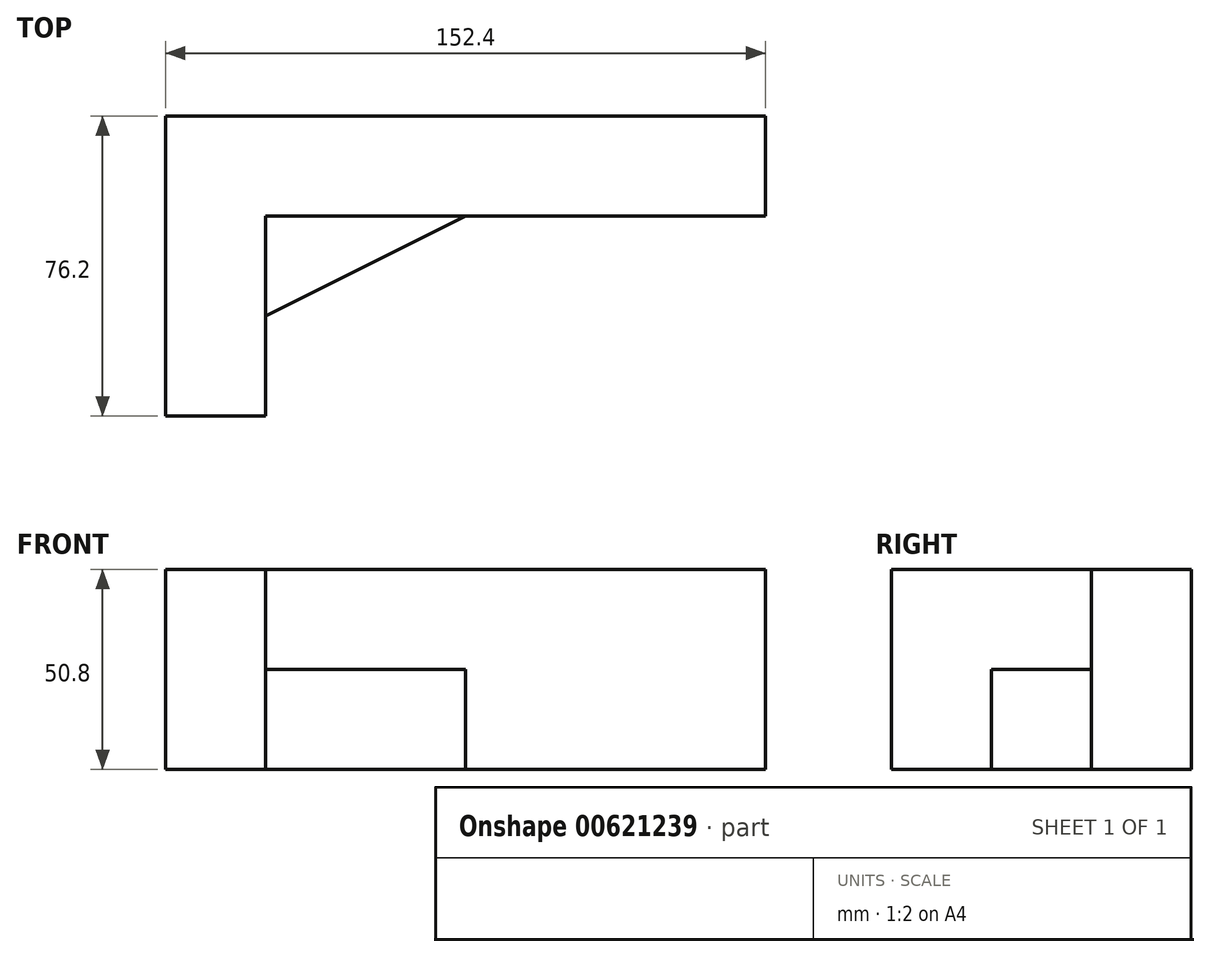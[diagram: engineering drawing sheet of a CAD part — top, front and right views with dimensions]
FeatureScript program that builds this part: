
annotation { "Feature Type Name" : "Feature", "Feature Type Description" : "" }
export const myFeature = defineFeature(function(context is Context, id is Id, definition is map)
    precondition{}
    {
        {
            var Q0;
            Q0=qCreatedBy(makeId("Front.planeOp"),FACE);
            var sketch = newSketch(context, id + "F0", { "sketchPlane" : qUnion([Q0])});
            skLineSegment(sketch, "E0", {"start": v(0, 50.8) * mm, "end": v(0, 0) * mm});
            skLineSegment(sketch, "E1", {"start": v(0, 0) * mm, "end": v(25.4, 0) * mm});
            skLineSegment(sketch, "E2", {"start": v(25.4, 0) * mm, "end": v(25.4, 50.8) * mm});
            skLineSegment(sketch, "E3", {"start": v(25.4, 50.8) * mm, "end": v(0, 50.8) * mm});
            skLineSegment(sketch, "E4", {"start": v(25.4, 50.8) * mm, "end": v(152.4, 50.8) * mm});
            skLineSegment(sketch, "E5", {"start": v(152.4, 50.8) * mm, "end": v(152.4, 0) * mm});
            skLineSegment(sketch, "E6", {"start": v(152.4, 0) * mm, "end": v(25.4, 0) * mm});
            skSolve(sketch);
        }
        {
            var Q0;
            Q0 = qSketchRegion(id + "F0", true);
            extrude(context, id + "F1", {"entities" : qUnion([Q0]), "depth" : 76.2 * mm, "offsetDistance" : 25.4 * mm});
        }
        {
            var Q0;
            Q0=makeQuery(id+"F1.opExtrude","SWEPT_FACE",FACE,{"disambiguationData":[OSD([sQuery(id+"F0.wireOp",EDGE,"E3"),sQuery(id+"F0.wireOp",EDGE,"E4")])]});
            var sketch = newSketch(context, id + "F2", { "sketchPlane" : qUnion([Q0])});
            skLineSegment(sketch, "E7", {"start": v(152.4, -76.2) * mm, "end": v(152.4, -25.4) * mm});
            skLineSegment(sketch, "E8", {"start": v(152.4, -25.4) * mm, "end": v(25.4, -25.4) * mm});
            skLineSegment(sketch, "E9", {"start": v(25.4, -25.4) * mm, "end": v(25.4, -76.2) * mm});
            skLineSegment(sketch, "E10", {"start": v(25.4, -76.2) * mm, "end": v(152.4, -76.2) * mm});
            skSolve(sketch);
        }
        {
            var Q0;
            Q0 = qSketchRegion(id + "F2", true);
            extrude(context, id + "F3", {"entities" : qUnion([Q0]), "operationType" : NewBodyOperationType.REMOVE, "oppositeDirection" : true, "depth" : 127 * mm, "offsetDistance" : 25.4 * mm});
        }
        {
            var Q0;
            Q0=makeQuery(id+"F3.boolean.opBoolean","COPY",FACE,{"derivedFrom":makeQuery(id+"F3.opExtrude","SWEPT_FACE",FACE,{"disambiguationData":[OSD([sQuery(id+"F2.wireOp",EDGE,"E8")])]})});
            var sketch = newSketch(context, id + "F4", { "sketchPlane" : qUnion([Q0])});
            skLineSegment(sketch, "E11", {"start": v(25.4, 0) * mm, "end": v(76.2, 0) * mm});
            skLineSegment(sketch, "E12", {"start": v(76.2, 0) * mm, "end": v(76.2, 25.4) * mm});
            skLineSegment(sketch, "E13", {"start": v(76.2, 25.4) * mm, "end": v(25.4, 25.4) * mm});
            skLineSegment(sketch, "E14", {"start": v(25.4, 25.4) * mm, "end": v(25.4, 0) * mm});
            skSolve(sketch);
        }
        {
            var Q0;
            Q0=makeQuery(id+"F4.imprint","IMPRINT",FACE,{"disambiguationData":[TD([[makeQuery(id+"F4.imprint","IMPRINT",EDGE,{"derivedFrom":sQuery(id+"F4.wireOp",EDGE,"E11")}),-1.0]])]});
            extrude(context, id + "F5", {"entities" : qUnion([Q0]), "operationType" : NewBodyOperationType.ADD, "depth" : 25.4 * mm, "offsetDistance" : 25.4 * mm});
        }
        {
            var Q0;
            Q0=makeQuery(id+"F5.opExtrude","SWEPT_FACE",FACE,{"disambiguationData":[OSD([sQuery(id+"F4.wireOp",EDGE,"E13")])]});
            var sketch = newSketch(context, id + "F6", { "sketchPlane" : qUnion([Q0])});
            skLineSegment(sketch, "E15", {"start": v(25.4, -50.8) * mm, "end": v(76.2, -25.4) * mm});
            skLineSegment(sketch, "E16", {"start": v(76.2, -25.4) * mm, "end": v(76.2, -50.8) * mm});
            skLineSegment(sketch, "E17", {"start": v(76.2, -50.8) * mm, "end": v(25.4, -50.8) * mm});
            skSolve(sketch);
        }
        {
            var Q0;
            Q0 = qSketchRegion(id + "F6", true);
            extrude(context, id + "F7", {"entities" : qUnion([Q0]), "operationType" : NewBodyOperationType.REMOVE, "oppositeDirection" : true, "depth" : 25.4 * mm, "offsetDistance" : 25.4 * mm});
        }
    });
